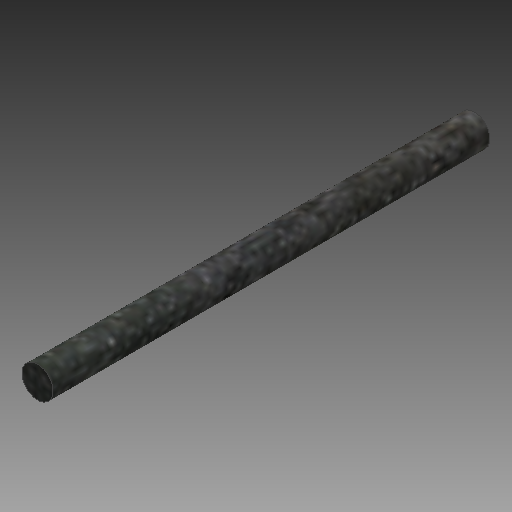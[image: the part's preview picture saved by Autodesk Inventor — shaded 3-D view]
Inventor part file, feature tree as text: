
AUTODESK INVENTOR PART (.ipt)
format: ipt  version: 2018 (Build 220112000, 112)  size: 117,248 bytes
history: native  units: mm
features: other x3, sketch x1
ambient origin geometry x8: Origin, YZ Plane, XZ Plane, XY Plane, X Axis, Y Axis, Z Axis, Center Point
bodies: Volumenkörper1 (feature_tree)
feature tree (4):
  other  "Metall Stab M5.ipt"
  other  "Volumenkörper1::Metall Stab M5.ipt"
  other  "Bezeichnung1"
  sketch  "Skizze1"  dims[d0=10.0mm]
